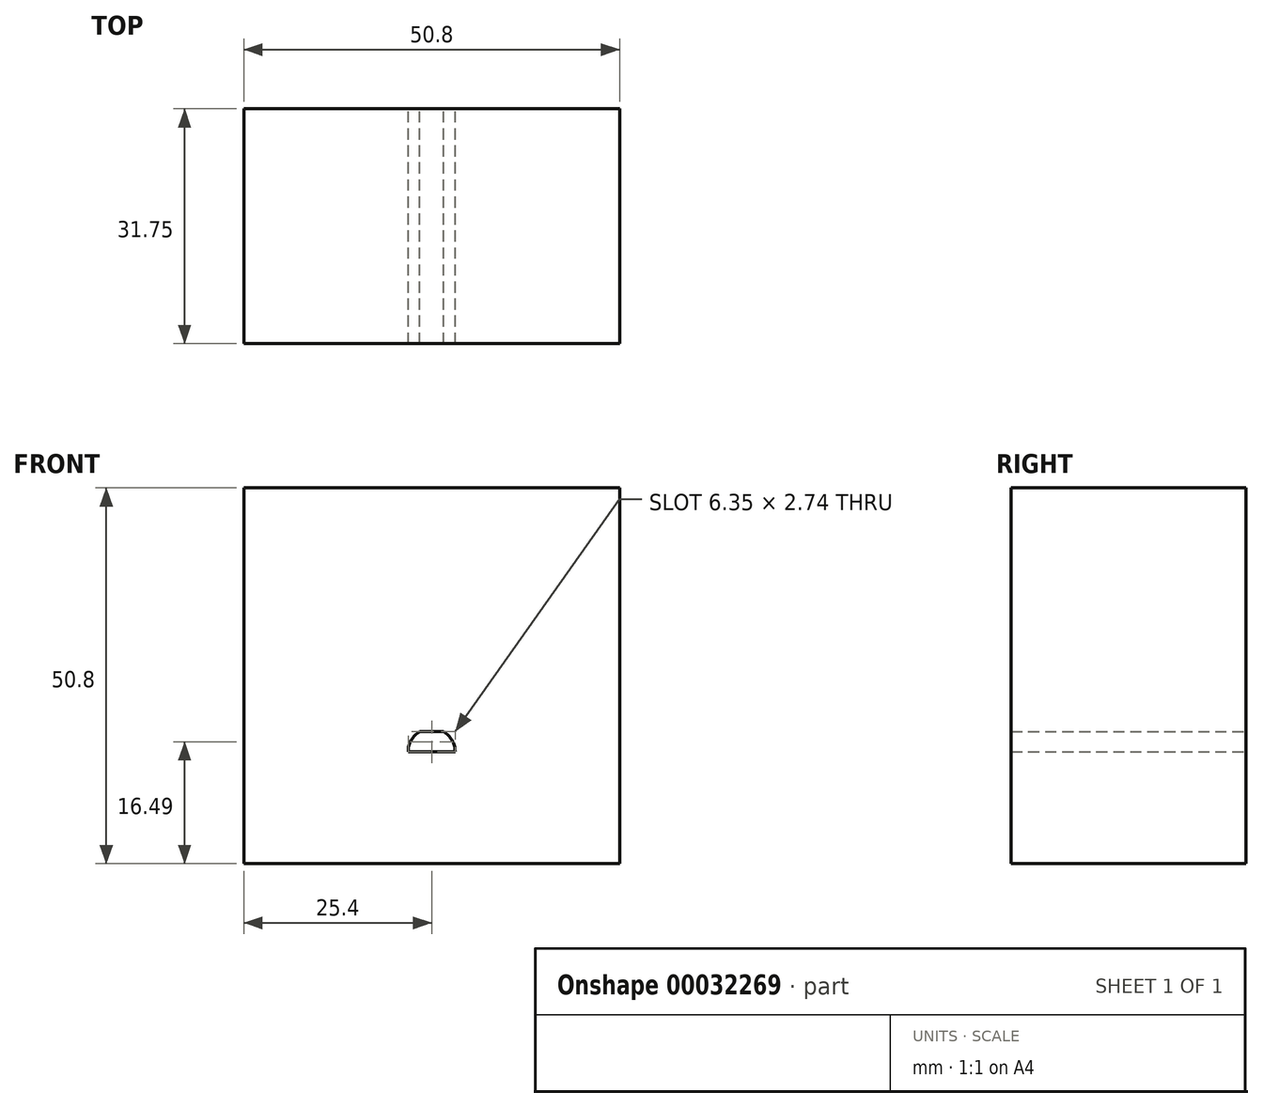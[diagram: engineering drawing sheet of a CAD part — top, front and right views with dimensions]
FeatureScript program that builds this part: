
annotation { "Feature Type Name" : "Feature", "Feature Type Description" : "" }
export const myFeature = defineFeature(function(context is Context, id is Id, definition is map)
    precondition{}
    {
        {
            var Q0;
            Q0=qCreatedBy(makeId("Front.planeOp"),FACE);
            var sketch = newSketch(context, id + "F0", { "sketchPlane" : qUnion([Q0])});
            skLineSegment(sketch, "E0", {"start": v(0, 0) * mm, "end": v(0, 50.8) * mm});
            skLineSegment(sketch, "E1", {"start": v(0, 50.8) * mm, "end": v(50.8, 50.8) * mm});
            skLineSegment(sketch, "E2", {"start": v(50.8, 50.8) * mm, "end": v(50.8, 0) * mm});
            skLineSegment(sketch, "E3", {"start": v(50.8, 0) * mm, "end": v(0, 0) * mm});
            skLineSegment(sketch, "E4", {"start": v(25.4, 0) * mm, "end": v(25.4, 15.12) * mm, "construction": true});
            skPoint(sketch, "E4.endSnap0", {"position": v(25.4, 0) * mm});
            skArc(sketch, "E5", {"start": v(23.8, 17.86) * mm, "mid": v(22.65, 16.7) * mm, "end": v(22.23, 15.12) * mm});
            skLineSegment(sketch, "E6", {"start": v(28.58, 15.12) * mm, "end": v(22.23, 15.12) * mm});
            skLineSegment(sketch, "E7.0", {"start": v(27, 17.86) * mm, "end": v(23.8, 17.86) * mm});
            skArc(sketch, "E8.trimOffspring", {"start": v(28.58, 15.12) * mm, "mid": v(28.15, 16.7) * mm, "end": v(27, 17.86) * mm});
            skSolve(sketch);
        }
        {
            var Q0;
            Q0=makeQuery(id+"F0.imprint","IMPRINT",FACE,{"disambiguationData":[TD([[makeQuery(id+"F0.imprint","IMPRINT",EDGE,{"derivedFrom":sQuery(id+"F0.wireOp",EDGE,"E0")}),-1.0]])]});
            extrude(context, id + "F1", {"entities" : qUnion([Q0]), "depth" : 31.75 * mm});
        }
    });
